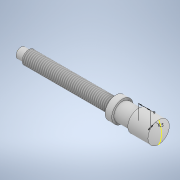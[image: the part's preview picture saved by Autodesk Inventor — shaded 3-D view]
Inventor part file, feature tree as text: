
AUTODESK INVENTOR PART (.ipt)
format: ipt  version: 2021 (Build 250183000, 183)  size: 136,704 bytes
history: native  units: mm
features: other x2, sketch x2, thread x1
ambient origin geometry x8: Origin, YZ Plane, XZ Plane, XY Plane, X Axis, Y Axis, Z Axis, Center Point
bodies: Body1 (feature_tree)
feature tree (5):
  other  "Sólido1"
  other  "Revolução1"
  thread  "Rosca1"  [1 undecoded]
  sketch  "Esboço3"  dims[d17=1.25mm d18=65.0mm d19=3.0mm d20=5.0mm d21=12.0mm d22=15.0mm d24=8.0mm d25=1.5mm d26=7.5mm d27=90.0deg d28=65.0mm d29=0.0mm d30=6.5mm d33=9.0mm d34=0.872665mm d35=0.5mm d36=0.872665mm]
  sketch  "Esboço1"  dims[d15=10.297443mm]
note: 1 required parameter value undecoded (feature->parameter linkage not recoverable at this tier; creation-order binding heuristic only, values carry confidence <= 0.55)
